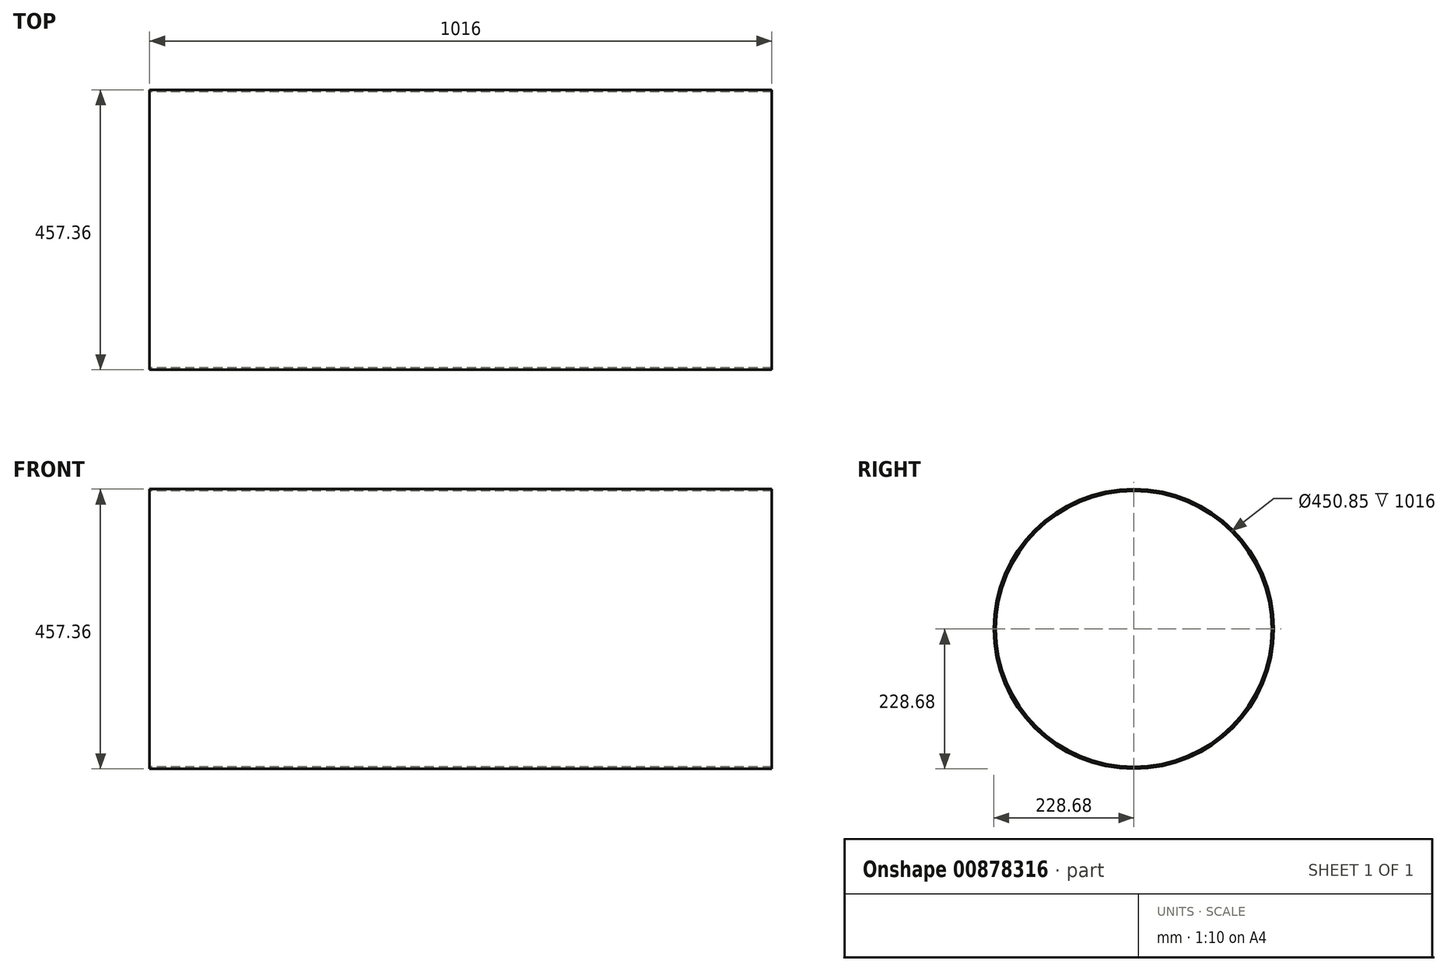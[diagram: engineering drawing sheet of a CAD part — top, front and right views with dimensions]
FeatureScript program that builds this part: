
annotation { "Feature Type Name" : "Feature", "Feature Type Description" : "" }
export const myFeature = defineFeature(function(context is Context, id is Id, definition is map)
    precondition{}
    {
        {
            var Q0;
            Q0=qCreatedBy(makeId("Right.planeOp"),FACE);
            var sketch = newSketch(context, id + "F0", { "sketchPlane" : qUnion([Q0])});
            skCircle(sketch, "E0", {"center": v(0, 0) * mm, "radius": 225.43 * mm});
            skCircle(sketch, "E1", {"center": v(0, 0) * mm, "radius": 228.68 * mm});
            skSolve(sketch);
        }
        {
            var Q0;
            Q0 = qSketchRegion(id + "F0", true);
            extrude(context, id + "F1", {"entities" : qUnion([Q0]), "depth" : 1016 * mm, "offsetDistance" : 25.4 * mm});
        }
    });
